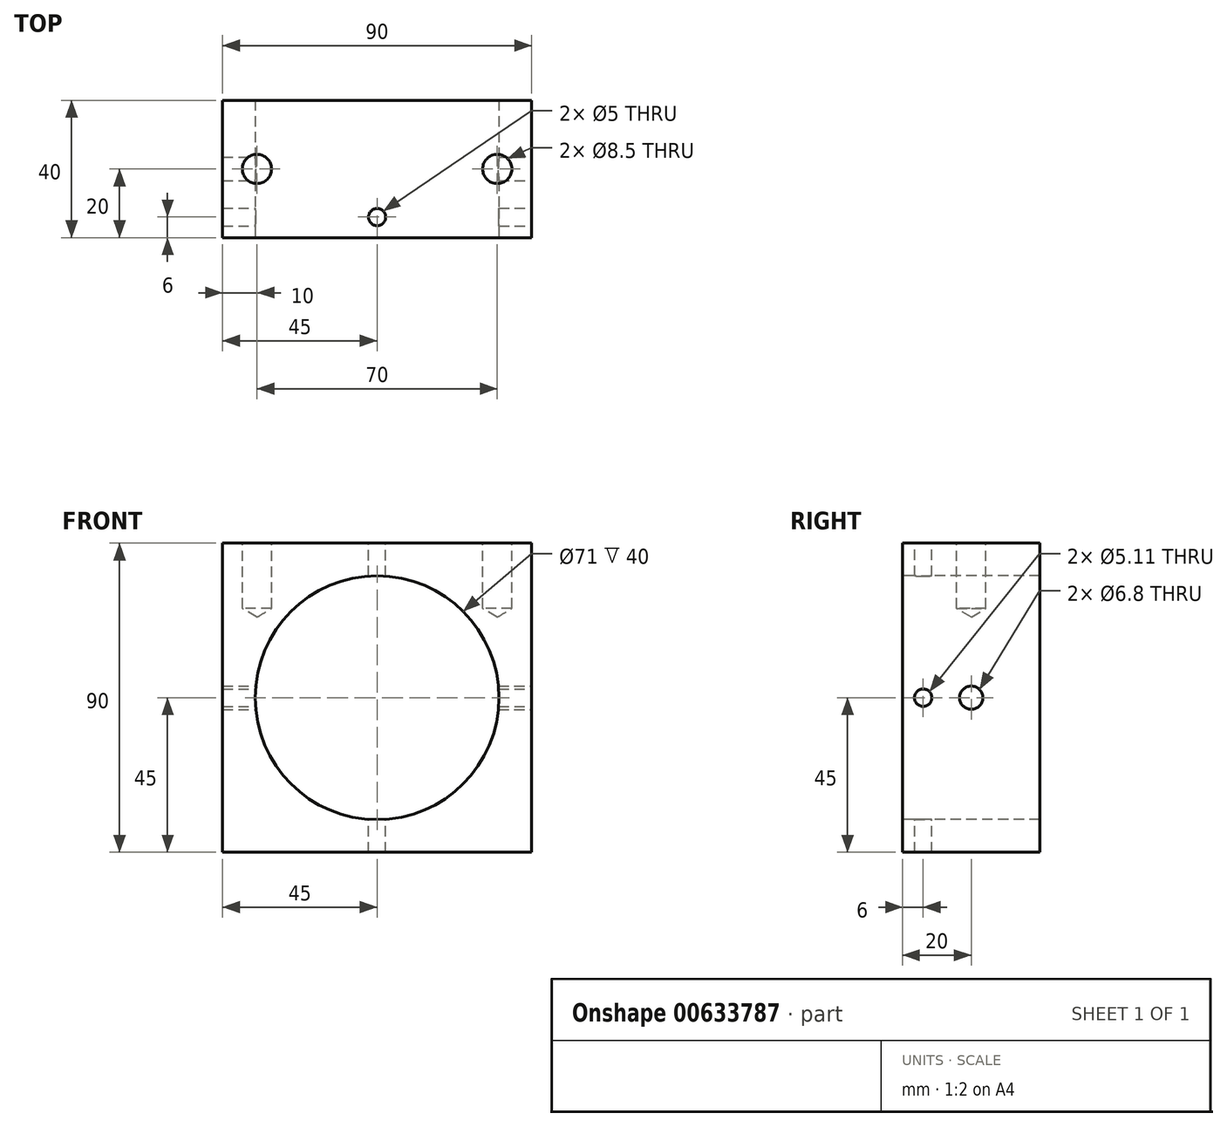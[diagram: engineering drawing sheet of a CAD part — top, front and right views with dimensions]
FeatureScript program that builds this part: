
annotation { "Feature Type Name" : "Feature", "Feature Type Description" : "" }
export const myFeature = defineFeature(function(context is Context, id is Id, definition is map)
    precondition{}
    {
        {
            var Q0;
            Q0=qCreatedBy(makeId("Front.planeOp"),FACE);
            var sketch = newSketch(context, id + "F0", { "sketchPlane" : qUnion([Q0])});
            skLineSegment(sketch, "E0.bottom", {"start": v(0, 0) * mm, "end": v(90, 0) * mm});
            skLineSegment(sketch, "E0.top", {"start": v(0, 90) * mm, "end": v(90, 90) * mm});
            skLineSegment(sketch, "E0.left", {"start": v(0, 0) * mm, "end": v(0, 90) * mm});
            skLineSegment(sketch, "E0.right", {"start": v(90, 0) * mm, "end": v(90, 90) * mm});
            skSolve(sketch);
        }
        {
            var Q0;
            Q0 = qSketchRegion(id + "F0", true);
            var Q1;
            Q1=makeQuery(id+"F0.imprint","IMPRINT",FACE,{"disambiguationData":[TD([[makeQuery(id+"F0.imprint","IMPRINT",EDGE,{"derivedFrom":sQuery(id+"F0.wireOp",EDGE,"E0.bottom")}),1.0]])]});
            extrude(context, id + "F1", {"entities" : qUnion([Q0, Q1]), "depth" : 40 * mm, "offsetDistance" : 25 * mm});
        }
        {
            var Q0;
            Q0=makeQuery(id+"F1.opExtrude","CAP_FACE",FACE,{"disambiguationData":[OSD([sQuery(id+"F0.wireOp",EDGE,"E0.bottom"),sQuery(id+"F0.wireOp",EDGE,"E0.top"),sQuery(id+"F0.wireOp",EDGE,"E0.left"),sQuery(id+"F0.wireOp",EDGE,"E0.right")])],"isStart":false});
            var sketch = newSketch(context, id + "F2", { "sketchPlane" : qUnion([Q0])});
            skPoint(sketch, "E1", {"position": v(45, 45) * mm});
            skPoint(sketch, "E1.positionSnap0", {"position": v(0, 45) * mm});
            skPoint(sketch, "E1.positionSnap1", {"position": v(45, 90) * mm});
            skSolve(sketch);
        }
        {
            var Q0;
            Q0=sQuery(id+"F2.wireOp",VERTEX,"E1");
            var Q1;
            Q1=makeQuery(id+"F1.opExtrude","SWEPT_BODY",BODY,{"disambiguationData":[OSD([sQuery(id+"F0.wireOp",EDGE,"E0.bottom"),sQuery(id+"F0.wireOp",EDGE,"E0.top"),sQuery(id+"F0.wireOp",EDGE,"E0.left"),sQuery(id+"F0.wireOp",EDGE,"E0.right")])]});
            hole(context, id + "F3", {"style" : HoleStyle.SIMPLE, "endStyle" : HoleEndStyle.THROUGH, "holeDiameter" : 71 * mm, "majorDiameter" : 5 * mm, "isTappedThrough" : true, "tappedDepth" : 8 * mm, "tapClearance" : 3, "startFromSketch" : true, "locations" : qUnion([Q0]), "scope" : qUnion([Q1])});
        }
        {
            var Q0;
            Q0=makeQuery(id+"F1.opExtrude","SWEPT_FACE",FACE,{"disambiguationData":[OSD([sQuery(id+"F0.wireOp",EDGE,"E0.right")])]});
            var sketch = newSketch(context, id + "F4", { "sketchPlane" : qUnion([Q0])});
            skPoint(sketch, "E2", {"position": v(-20, 45) * mm});
            skPoint(sketch, "E2.positionSnap0", {"position": v(-40, 45) * mm});
            skPoint(sketch, "E3", {"position": v(-34, 45) * mm});
            skSolve(sketch);
        }
        {
            var Q0;
            Q0=sQuery(id+"F4.wireOp",VERTEX,"E3");
            var Q1;
            Q1=makeQuery(id+"F1.opExtrude","SWEPT_BODY",BODY,{"disambiguationData":[OSD([sQuery(id+"F0.wireOp",EDGE,"E0.bottom"),sQuery(id+"F0.wireOp",EDGE,"E0.top"),sQuery(id+"F0.wireOp",EDGE,"E0.left"),sQuery(id+"F0.wireOp",EDGE,"E0.right")])]});
            hole(context, id + "F5", {"style" : HoleStyle.SIMPLE, "endStyle" : HoleEndStyle.THROUGH, "standardTappedOrClearance" : lookupTablePath({ "standard" : "ANSI", "engagement" : "75%", "pitch" : "20 tpi", "size" : "1/4", "type" : "Tapped" }), "standardBlindInLast" : lookupTablePath({ "standard" : "ANSI", "engagement" : "75%", "pitch" : "20 tpi", "size" : "1/4", "type" : "Tapped" }), "holeDiameter" : 5.1 * mm, "majorDiameter" : 6.35 * mm, "showTappedDepth" : true, "isTappedThrough" : true, "tappedDepth" : 8 * mm, "tapClearance" : 3, "startFromSketch" : true, "locations" : qUnion([Q0]), "scope" : qUnion([Q1])});
        }
        {
            var Q0;
            Q0=sQuery(id+"F4.wireOp",VERTEX,"E2");
            var Q1;
            Q1=makeQuery(id+"F1.opExtrude","SWEPT_BODY",BODY,{"disambiguationData":[OSD([sQuery(id+"F0.wireOp",EDGE,"E0.bottom"),sQuery(id+"F0.wireOp",EDGE,"E0.top"),sQuery(id+"F0.wireOp",EDGE,"E0.left"),sQuery(id+"F0.wireOp",EDGE,"E0.right")])]});
            hole(context, id + "F6", {"style" : HoleStyle.SIMPLE, "endStyle" : HoleEndStyle.THROUGH, "standardTappedOrClearance" : lookupTablePath({ "standard" : "ISO", "engagement" : "75%", "pitch" : "1.25 mm", "size" : "M8", "type" : "Tapped" }), "standardBlindInLast" : lookupTablePath({ "standard" : "ISO", "engagement" : "75%", "pitch" : "1.25 mm", "size" : "M8", "type" : "Tapped" }), "holeDiameter" : 6.8 * mm, "majorDiameter" : 8 * mm, "showTappedDepth" : true, "isTappedThrough" : true, "tappedDepth" : 8 * mm, "tapClearance" : 3, "startFromSketch" : true, "locations" : qUnion([Q0]), "scope" : qUnion([Q1])});
        }
        {
            var Q0;
            Q0=makeQuery(id+"F1.opExtrude","SWEPT_FACE",FACE,{"disambiguationData":[OSD([sQuery(id+"F0.wireOp",EDGE,"E0.top")])]});
            var sketch = newSketch(context, id + "F7", { "sketchPlane" : qUnion([Q0])});
            skPoint(sketch, "E4", {"position": v(45, -34) * mm});
            skPoint(sketch, "E4.positionSnap0", {"position": v(45, -40) * mm});
            skSolve(sketch);
        }
        {
            var Q0;
            Q0=sQuery(id+"F7.wireOp",VERTEX,"813ffbfc-0480-40bf-812b-e1b9a5abd96c");
            var Q1;
            Q1=sQuery(id+"F7.wireOp",VERTEX,"E4");
            var Q2;
            Q2=sQuery(id+"F7.wireOp",VERTEX,"829b73ba-a39f-4cfc-bcea-5b68b1ca6298");
            var Q3;
            Q3=makeQuery(id+"F1.opExtrude","SWEPT_BODY",BODY,{"disambiguationData":[OSD([sQuery(id+"F0.wireOp",EDGE,"E0.bottom"),sQuery(id+"F0.wireOp",EDGE,"E0.top"),sQuery(id+"F0.wireOp",EDGE,"E0.left"),sQuery(id+"F0.wireOp",EDGE,"E0.right")])]});
            hole(context, id + "F8", {"style" : HoleStyle.SIMPLE, "endStyle" : HoleEndStyle.THROUGH, "holeDiameter" : 5 * mm, "majorDiameter" : 6 * mm, "isTappedThrough" : true, "tappedDepth" : 8 * mm, "tapClearance" : 3, "startFromSketch" : true, "locations" : qUnion([Q0, Q1, Q2]), "scope" : qUnion([Q3])});
        }
        {
            var Q0;
            {var subQ0=sQuery(id+"F0.wireOp",EDGE,"E0.top");Q0=makeQuery(id+"F7.imprint","IMPRINT",FACE,{"disambiguationData":[TD([[makeQuery(id+"F7.imprint","IMPRINT",EDGE,{"derivedFrom":makeQuery(id+"F1.opExtrude","CAP_EDGE",EDGE,{"disambiguationData":[OSD([subQ0])],"isStart":true})}),-1.0]])]});}
            var sketch = newSketch(context, id + "F9", { "sketchPlane" : qUnion([Q0])});
            skPoint(sketch, "E5", {"position": v(10, -20) * mm});
            skPoint(sketch, "E6", {"position": v(80, -20) * mm});
            skSolve(sketch);
        }
        {
            var Q0;
            Q0=sQuery(id+"F9.wireOp",VERTEX,"E5");
            var Q1;
            Q1=sQuery(id+"F9.wireOp",VERTEX,"E6");
            var Q2;
            Q2=makeQuery(id+"F1.opExtrude","SWEPT_BODY",BODY,{"disambiguationData":[OSD([sQuery(id+"F0.wireOp",EDGE,"E0.bottom"),sQuery(id+"F0.wireOp",EDGE,"E0.top"),sQuery(id+"F0.wireOp",EDGE,"E0.left"),sQuery(id+"F0.wireOp",EDGE,"E0.right")])]});
            hole(context, id + "F10", {"style" : HoleStyle.SIMPLE, "endStyle" : HoleEndStyle.BLIND, "standardTappedOrClearance" : lookupTablePath({ "standard" : "ISO", "engagement" : "75%", "pitch" : "1.5 mm", "size" : "M10", "type" : "Tapped" }), "standardBlindInLast" : lookupTablePath({ "standard" : "ISO", "engagement" : "75%", "pitch" : "1.5 mm", "size" : "M10", "type" : "Tapped" }), "holeDiameter" : 8.5 * mm, "majorDiameter" : 10 * mm, "showTappedDepth" : true, "holeDepth" : 19 * mm, "isTappedThrough" : true, "tappedDepth" : 14.5 * mm, "tapClearance" : 3, "startFromSketch" : true, "locations" : qUnion([Q0, Q1]), "scope" : qUnion([Q2])});
        }
    });
